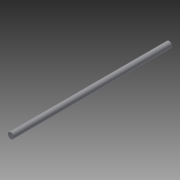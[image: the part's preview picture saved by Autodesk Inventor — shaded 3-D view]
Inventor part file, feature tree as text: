
AUTODESK INVENTOR PART (.ipt)
format: ipt  version: 2013 (Build 170138000, 138)  size: 63,488 bytes
history: native  units: in
note: dims shown in document units (in); Inventor stores cm internally (conversion verified against a paired STEP export)
features: extrude x1, sketch x1
ambient origin geometry x8: Origin, YZ Plane, XZ Plane, XY Plane, X Axis, Y Axis, Z Axis, Center Point
bodies: Solid1 (feature_tree)
feature tree (2):
  extrude  "Extrusion1"  Depth=40.0in TaperAngle=0.0deg
  sketch  "Sketch1"  dims[d0=1.5in d1=40.0in d2=0.0in]
